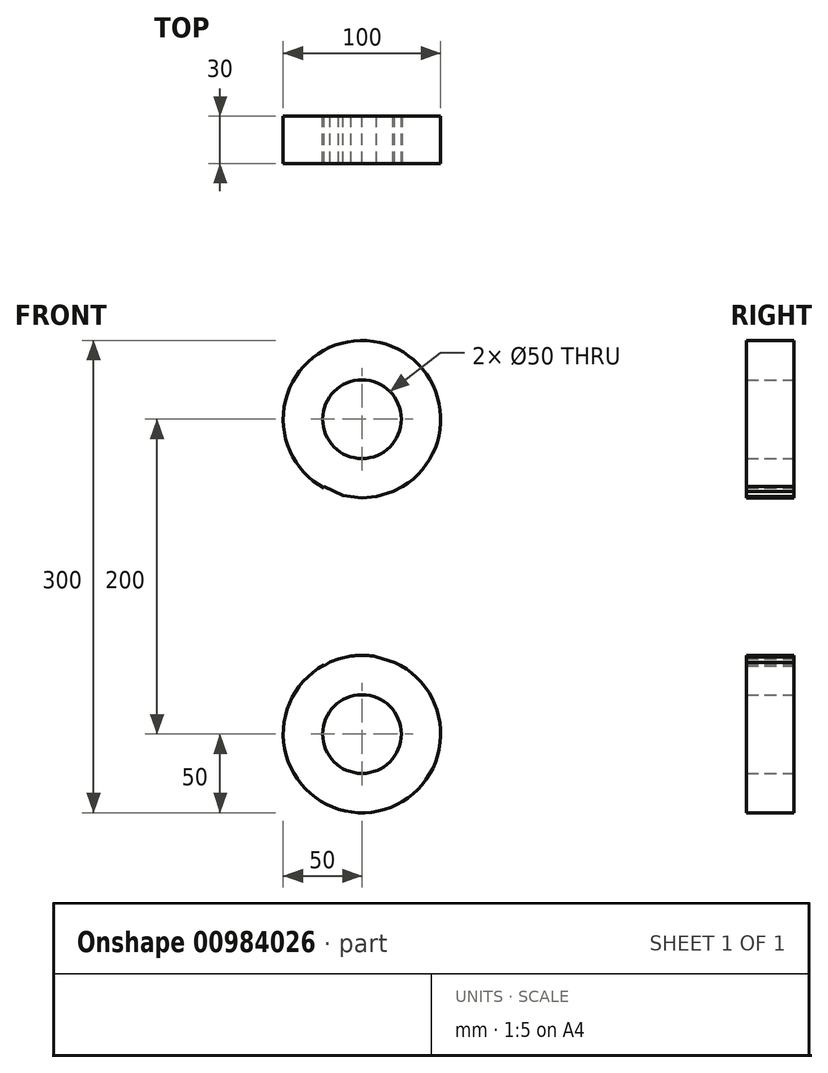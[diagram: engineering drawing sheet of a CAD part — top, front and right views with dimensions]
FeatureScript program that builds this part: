
annotation { "Feature Type Name" : "Feature", "Feature Type Description" : "" }
export const myFeature = defineFeature(function(context is Context, id is Id, definition is map)
    precondition{}
    {
        {
            var Q0;
            Q0=qCreatedBy(makeId("Front.planeOp"),FACE);
            var sketch = newSketch(context, id + "F0", { "sketchPlane" : qUnion([Q0])});
            skCircle(sketch, "E0", {"center": v(0, 0) * mm, "radius": 50 * mm});
            skCircle(sketch, "E1", {"center": v(0, 0) * mm, "radius": 25 * mm});
            skCircle(sketch, "E2", {"center": v(0, -200) * mm, "radius": 25 * mm});
            skCircle(sketch, "E3", {"center": v(0, -200) * mm, "radius": 50 * mm});
            skSolve(sketch);
        }
        {
            var Q0;
            Q0=qCreatedBy(makeId("Front.planeOp"),FACE);
            var sketch = newSketch(context, id + "F1", { "sketchPlane" : qUnion([Q0])});
            skLineSegment(sketch, "E4", {"start": v(-24.1, -42.81) * mm, "end": v(-24.1, -156.81) * mm});
            skLineSegment(sketch, "E5", {"start": v(25.8, -156.81) * mm, "end": v(25.8, -42.81) * mm});
            skSolve(sketch);
        }
        {
            var Q0;
            Q0=qCreatedBy(makeId("Front.planeOp"),FACE);
            var sketch = newSketch(context, id + "F2", { "sketchPlane" : qUnion([Q0])});
            skCircle(sketch, "E6.0", {"center": v(0, 0) * mm, "radius": 50 * mm});
            skCircle(sketch, "E7.0", {"center": v(0, -200) * mm, "radius": 50 * mm});
            skLineSegment(sketch, "E8.0", {"start": v(25.8, -156.81) * mm, "end": v(25.8, -42.81) * mm});
            skLineSegment(sketch, "E8.1", {"start": v(-24.1, -42.81) * mm, "end": v(-24.1, -156.81) * mm});
            skLineSegment(sketch, "E9", {"start": v(-24.1, -42.81) * mm, "end": v(-11.97, -48.55) * mm});
            skLineSegment(sketch, "E10", {"start": v(-11.97, -48.55) * mm, "end": v(0, -50) * mm});
            skLineSegment(sketch, "E11", {"start": v(0, -50) * mm, "end": v(9.35, -49.12) * mm});
            skLineSegment(sketch, "E12", {"start": v(9.35, -49.12) * mm, "end": v(19.66, -45.97) * mm});
            skLineSegment(sketch, "E13", {"start": v(19.66, -45.97) * mm, "end": v(25.8, -42.81) * mm});
            skLineSegment(sketch, "E14", {"start": v(25.8, -156.81) * mm, "end": v(20.76, -154.51) * mm});
            skLineSegment(sketch, "E15", {"start": v(20.76, -154.51) * mm, "end": v(9.35, -150.88) * mm});
            skLineSegment(sketch, "E16", {"start": v(9.35, -150.88) * mm, "end": v(0, -149.1) * mm});
            skLineSegment(sketch, "E17", {"start": v(0, -149.1) * mm, "end": v(-7.06, -150.5) * mm});
            skLineSegment(sketch, "E18", {"start": v(-7.06, -150.5) * mm, "end": v(-14.91, -152.28) * mm});
            skLineSegment(sketch, "E19", {"start": v(-14.91, -152.28) * mm, "end": v(-20.35, -154.33) * mm});
            skLineSegment(sketch, "E20", {"start": v(-20.35, -154.33) * mm, "end": v(-24.1, -156.81) * mm});
            skSolve(sketch);
        }
        {
            var Q0;
            {var subQ0=sQuery(id+"F2.wireOp",EDGE,"E15");Q0=makeQuery(id+"F2.imprint","IMPRINT",FACE,{"disambiguationData":[TD([[makeQuery(id+"F2.imprint","IMPRINT",EDGE,{"derivedFrom":subQ0}),1.0]])]});}
            var Q1;
            {var subQ0=sQuery(id+"F2.wireOp",EDGE,"E9");Q1=makeQuery(id+"F2.imprint","IMPRINT",FACE,{"disambiguationData":[TD([[makeQuery(id+"F2.imprint","IMPRINT",EDGE,{"derivedFrom":subQ0}),1.0]])]});}
            extrude(context, id + "F3", {"entities" : qUnion([Q0, Q1]), "depth" : 30 * mm, "offsetDistance" : 25 * mm});
        }
        {
            var Q0;
            Q0=sQuery(id+"F0.wireOp",VERTEX,"E0.center");
            var Q1;
            Q1=sQuery(id+"F0.wireOp",VERTEX,"E2.center");
            var Q2;
            Q2=makeQuery(id+"F3.opExtrude","SWEPT_BODY",BODY,{"disambiguationData":[OSD([sQuery(id+"F2.wireOp",EDGE,"E6.0"),sQuery(id+"F2.wireOp",EDGE,"E8.0"),sQuery(id+"F2.wireOp",EDGE,"E8.1"),sQuery(id+"F2.wireOp",EDGE,"E9"),sQuery(id+"F2.wireOp",EDGE,"E10"),sQuery(id+"F2.wireOp",EDGE,"E11"),sQuery(id+"F2.wireOp",EDGE,"E12"),sQuery(id+"F2.wireOp",EDGE,"E13")])]});
            var Q3;
            Q3=makeQuery(id+"F3.opExtrude","SWEPT_BODY",BODY,{"disambiguationData":[OSD([sQuery(id+"F2.wireOp",EDGE,"E7.0"),sQuery(id+"F2.wireOp",EDGE,"E8.1"),sQuery(id+"F2.wireOp",EDGE,"E15"),sQuery(id+"F2.wireOp",EDGE,"E18"),sQuery(id+"F2.wireOp",EDGE,"E19"),sQuery(id+"F2.wireOp",EDGE,"E20")])]});
            hole(context, id + "F4", {"style" : HoleStyle.SIMPLE, "endStyle" : HoleEndStyle.THROUGH, "oppositeDirection" : true, "holeDiameter" : 50 * mm, "majorDiameter" : 5 * mm, "isTappedThrough" : true, "tappedDepth" : 12 * mm, "tapClearance" : 3, "locations" : qUnion([Q0, Q1]), "scope" : qUnion([Q2, Q3])});
        }
    });
